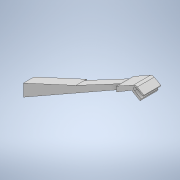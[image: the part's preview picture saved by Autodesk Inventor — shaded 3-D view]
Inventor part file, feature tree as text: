
AUTODESK INVENTOR PART (.ipt)
format: ipt  version: 2021 (Build 250183000, 183)  size: 181,760 bytes
history: native  units: mm
features: extrude x3, sketch x3, mirror x1
ambient origin geometry x8: Origin, YZ Plane, XZ Plane, XY Plane, X Axis, Y Axis, Z Axis, Center Point
bodies: Solid1 (feature_tree)
feature tree (7):
  extrude  "Extrusion1"  Depth=279.931505mm
  extrude  "Extrusion2"  Depth=4.336878mm
  mirror  "Mirror1"
  extrude  "Extrusion3"  Depth=10.0mm
  sketch  "Sketch1"  dims[d7=588.239625mm d8=279.931505mm]
  sketch  "Sketch2"  dims[d9=5.165078mm d10=4.336878mm]
  sketch  "Sketch3"  dims[d11=4.88916mm d12=5.376748mm d13=248.002124mm d14=211.001419mm d15=171.972718mm d16=284.224916mm d17=316.226348mm d18=60.0deg d19=26.17928mm d20=312.190756mm d21=15.707979mm d22=15.707948mm d23=90.0deg d24=21.124696mm d25=17.260897mm d26=12.172251mm d27=10.567205mm d28=12.649124mm d29=9.995658mm d30=18.294689mm d31=80.0mm d32=0.0mm d33=10.330604mm d34=20.0mm d35=0.0mm d36=10.0mm d37=0.0mm]
